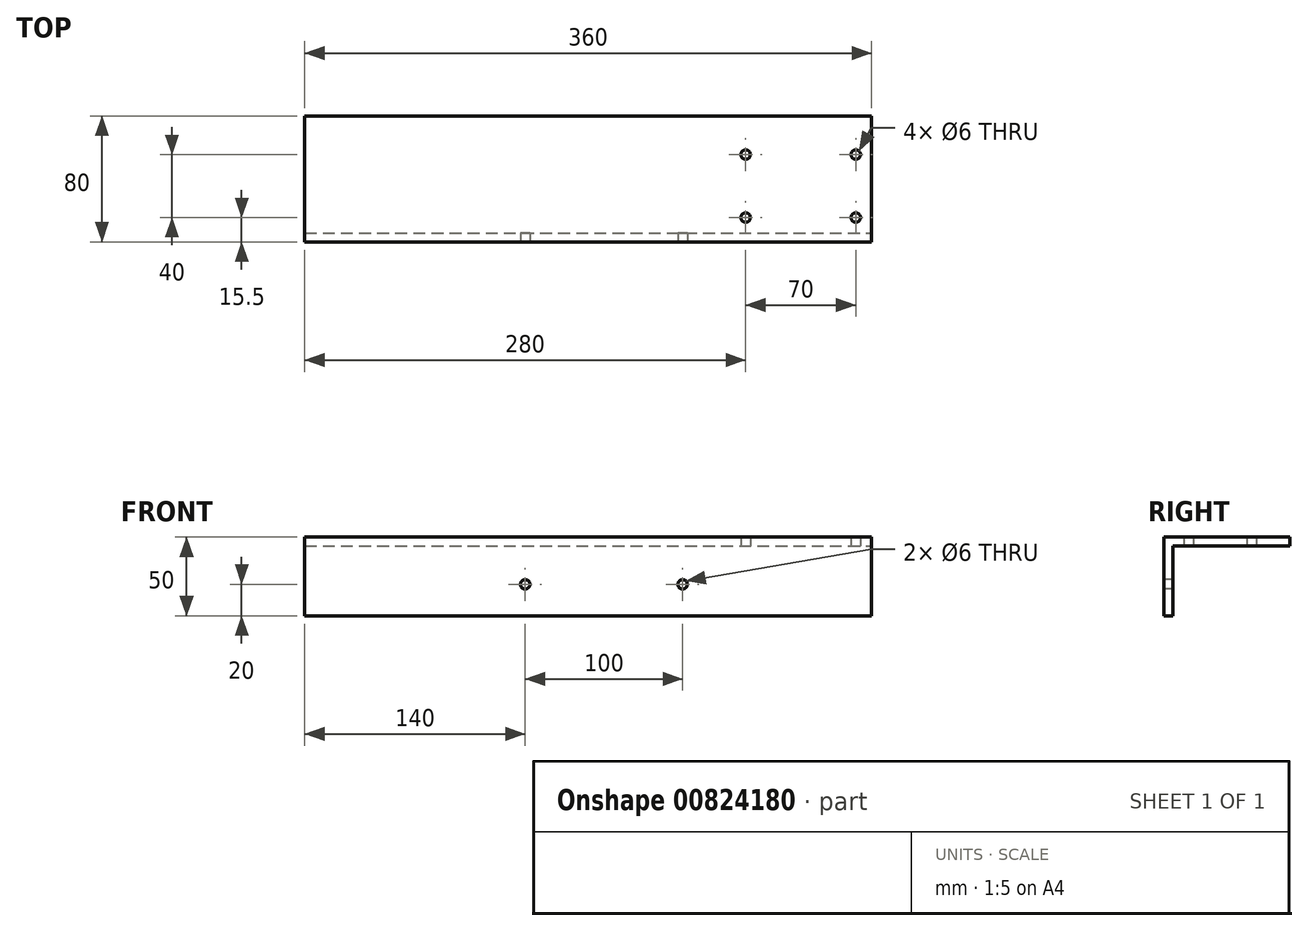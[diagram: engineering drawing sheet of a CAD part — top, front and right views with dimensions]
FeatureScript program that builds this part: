
annotation { "Feature Type Name" : "Feature", "Feature Type Description" : "" }
export const myFeature = defineFeature(function(context is Context, id is Id, definition is map)
    precondition{}
    {
        {
            var Q0;
            Q0=qCreatedBy(makeId("Top.planeOp"),FACE);
            var sketch = newSketch(context, id + "F0", { "sketchPlane" : qUnion([Q0])});
            skLineSegment(sketch, "E0.bottom", {"start": v(0, 0) * mm, "end": v(360, 0) * mm});
            skLineSegment(sketch, "E0.top", {"start": v(0, 80) * mm, "end": v(360, 80) * mm});
            skLineSegment(sketch, "E0.left", {"start": v(0, 0) * mm, "end": v(0, 80) * mm});
            skLineSegment(sketch, "E0.right", {"start": v(360, 0) * mm, "end": v(360, 80) * mm});
            skSolve(sketch);
        }
        {
            var Q0;
            Q0 = qSketchRegion(id + "F0", true);
            extrude(context, id + "F1", {"entities" : qUnion([Q0]), "depth" : 5.5 * mm, "offsetDistance" : 25 * mm});
        }
        {
            var Q0;
            Q0=makeQuery(id+"F1.opExtrude","CAP_FACE",FACE,{"disambiguationData":[OSD([sQuery(id+"F0.wireOp",EDGE,"E0.bottom"),sQuery(id+"F0.wireOp",EDGE,"E0.top"),sQuery(id+"F0.wireOp",EDGE,"E0.left"),sQuery(id+"F0.wireOp",EDGE,"E0.right")])],"isStart":true});
            var sketch = newSketch(context, id + "F2", { "sketchPlane" : qUnion([Q0])});
            skLineSegment(sketch, "E1.bottom", {"start": v(0, 0) * mm, "end": v(360, 0) * mm});
            skLineSegment(sketch, "E1.top", {"start": v(0, -5.5) * mm, "end": v(360, -5.5) * mm});
            skLineSegment(sketch, "E1.left", {"start": v(0, 0) * mm, "end": v(0, -5.5) * mm});
            skLineSegment(sketch, "E1.right", {"start": v(360, 0) * mm, "end": v(360, -5.5) * mm});
            skSolve(sketch);
        }
        {
            var Q0;
            Q0 = qSketchRegion(id + "F2", true);
            extrude(context, id + "F3", {"entities" : qUnion([Q0]), "operationType" : NewBodyOperationType.ADD, "depth" : 44.5 * mm, "offsetDistance" : 25 * mm});
        }
        {
            var Q0;
            Q0=makeQuery(id+"F3.boolean.opBoolean","MERGE",FACE,{"derivedFrom":[makeQuery(id+"F1.opExtrude","SWEPT_FACE",FACE,{"disambiguationData":[OSD([sQuery(id+"F0.wireOp",EDGE,"E0.bottom")])]}),makeQuery(id+"F3.opExtrude","SWEPT_FACE",FACE,{"disambiguationData":[OSD([sQuery(id+"F2.wireOp",EDGE,"E1.bottom")])]})]});
            var sketch = newSketch(context, id + "F4", { "sketchPlane" : qUnion([Q0])});
            skLineSegment(sketch, "E2", {"start": v(0, -24.5) * mm, "end": v(360, -24.5) * mm, "construction": true});
            skCircle(sketch, "E3", {"center": v(140, -24.5) * mm, "radius": 3 * mm});
            skCircle(sketch, "E4", {"center": v(240, -24.5) * mm, "radius": 3 * mm});
            skSolve(sketch);
        }
        {
            var Q0;
            Q0 = qSketchRegion(id + "F4", true);
            extrude(context, id + "F5", {"entities" : qUnion([Q0]), "operationType" : NewBodyOperationType.REMOVE, "oppositeDirection" : true, "depth" : 25 * mm, "offsetDistance" : 25 * mm});
        }
        {
            var Q0;
            Q0=makeQuery(id+"F1.opExtrude","CAP_FACE",FACE,{"disambiguationData":[OSD([sQuery(id+"F0.wireOp",EDGE,"E0.bottom"),sQuery(id+"F0.wireOp",EDGE,"E0.top"),sQuery(id+"F0.wireOp",EDGE,"E0.left"),sQuery(id+"F0.wireOp",EDGE,"E0.right")])],"isStart":true});
            var sketch = newSketch(context, id + "F6", { "sketchPlane" : qUnion([Q0])});
            skLineSegment(sketch, "E5", {"start": v(360, -15.5) * mm, "end": v(220.1, -15.5) * mm, "construction": true});
            skLineSegment(sketch, "E6", {"start": v(280, -80) * mm, "end": v(280, -10.1) * mm, "construction": true});
            skLineSegment(sketch, "E7", {"start": v(350, -80) * mm, "end": v(350, -10.1) * mm, "construction": true});
            skLineSegment(sketch, "E8", {"start": v(360, -55.5) * mm, "end": v(220.1, -55.5) * mm, "construction": true});
            skCircle(sketch, "E9", {"center": v(280, -15.5) * mm, "radius": 3 * mm});
            skCircle(sketch, "E10", {"center": v(280, -55.5) * mm, "radius": 3 * mm});
            skCircle(sketch, "E11", {"center": v(350, -55.5) * mm, "radius": 3 * mm});
            skCircle(sketch, "E12", {"center": v(350, -15.5) * mm, "radius": 3 * mm});
            skSolve(sketch);
        }
        {
            var Q0;
            Q0 = qSketchRegion(id + "F6", true);
            extrude(context, id + "F7", {"entities" : qUnion([Q0]), "operationType" : NewBodyOperationType.REMOVE, "oppositeDirection" : true, "depth" : 25 * mm, "offsetDistance" : 25 * mm});
        }
    });
